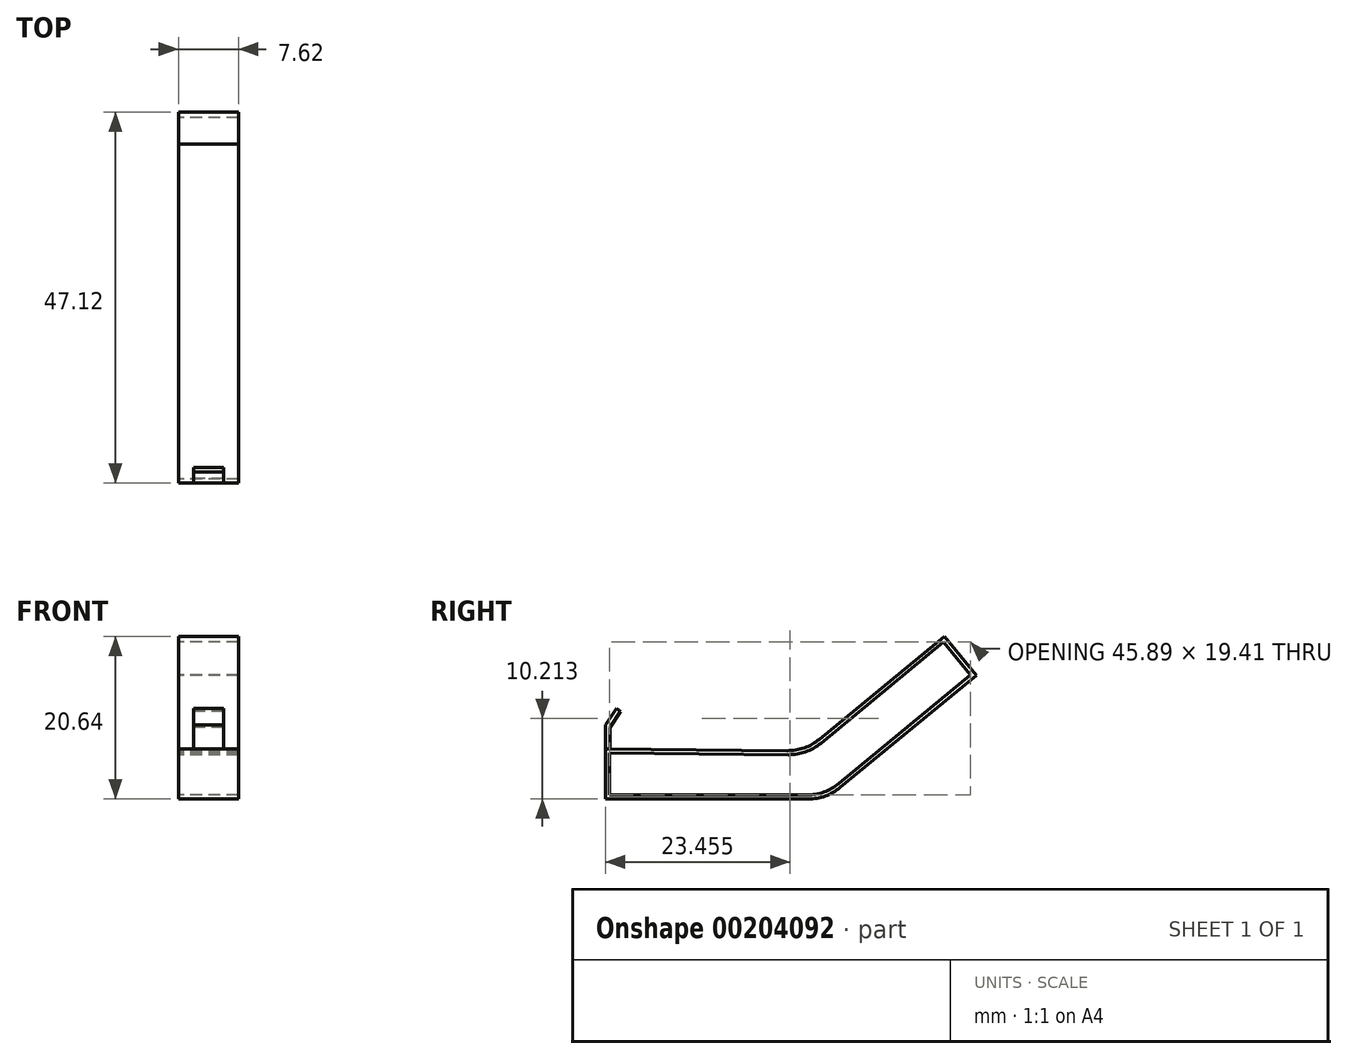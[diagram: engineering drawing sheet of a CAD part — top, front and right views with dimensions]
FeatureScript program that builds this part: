
annotation { "Feature Type Name" : "Feature", "Feature Type Description" : "" }
export const myFeature = defineFeature(function(context is Context, id is Id, definition is map)
    precondition{}
    {
        {
            var Q0;
            Q0=qCreatedBy(makeId("Right.planeOp"),FACE);
            var sketch = newSketch(context, id + "F0", { "sketchPlane" : qUnion([Q0])});
            skLineSegment(sketch, "E0", {"start": v(0, 0) * mm, "end": v(0, 6.35) * mm});
            skLineSegment(sketch, "E1", {"start": v(0, 6.35) * mm, "end": v(23.09, 6.13) * mm});
            skLineSegment(sketch, "E2", {"start": v(27.18, 7.58) * mm, "end": v(43.05, 20.64) * mm});
            skLineSegment(sketch, "E3", {"start": v(0, 0) * mm, "end": v(25.79, 0) * mm});
            skLineSegment(sketch, "E4", {"start": v(29.83, 1.45) * mm, "end": v(47.12, 15.69) * mm});
            skLineSegment(sketch, "E5", {"start": v(43.05, 20.64) * mm, "end": v(47.12, 15.69) * mm});
            skLineSegment(sketch, "E6.0", {"start": v(0, 5.84) * mm, "end": v(0, 5.84) * mm});
            skLineSegment(sketch, "E7.0", {"start": v(0.5, 0.5) * mm, "end": v(0.5, 5.84) * mm});
            skLineSegment(sketch, "E8.0", {"start": v(0.5, 0.5) * mm, "end": v(25.6, 0.5) * mm});
            skLineSegment(sketch, "E9.0", {"start": v(29.64, 1.96) * mm, "end": v(46.4, 15.75) * mm});
            skLineSegment(sketch, "E10.0", {"start": v(27.36, 7.07) * mm, "end": v(42.97, 19.92) * mm});
            skLineSegment(sketch, "E11.trimOffspring", {"start": v(0.5, 5.84) * mm, "end": v(23.27, 5.62) * mm});
            skLineSegment(sketch, "E12.trimOffspring", {"start": v(0.5, 6.35) * mm, "end": v(0.5, 6.35) * mm});
            skLineSegment(sketch, "E13", {"start": v(42.97, 19.92) * mm, "end": v(46.4, 15.75) * mm});
            skPoint(sketch, "E14.visualSharp", {"position": v(25.58, 5.6) * mm});
            skArc(sketch, "E14.filletArc", {"start": v(23.27, 5.62) * mm, "mid": v(25.44, 5.98) * mm, "end": v(27.36, 7.07) * mm});
            skPoint(sketch, "E15.visualSharp", {"position": v(25.4, 6.11) * mm});
            skArc(sketch, "E15.filletArc", {"start": v(23.09, 6.13) * mm, "mid": v(25.26, 6.5) * mm, "end": v(27.18, 7.58) * mm});
            skPoint(sketch, "E16.visualSharp", {"position": v(27.88, 0.5) * mm});
            skArc(sketch, "E16.filletArc", {"start": v(25.6, 0.5) * mm, "mid": v(27.75, 0.88) * mm, "end": v(29.64, 1.96) * mm});
            skPoint(sketch, "E17.visualSharp", {"position": v(28.07, 0) * mm});
            skArc(sketch, "E17.filletArc", {"start": v(25.79, 0) * mm, "mid": v(27.93, 0.37) * mm, "end": v(29.83, 1.45) * mm});
            skSolve(sketch);
        }
        {
            var Q0;
            Q0=qSketchRegion(id+"F0",true);
            var Q1;
            {var subQ3=sQuery(id+"F0.wireOp",EDGE,"E2");Q1=makeQuery(id+"F0.imprint","IMPRINT",FACE,{"disambiguationData":[TD([[makeQuery(id+"F0.imprint","IMPRINT",EDGE,{"derivedFrom":subQ3}),-1.0]])]});}
            extrude(context, id + "F1", {"entities" : qUnion([Q0, Q1]), "endBound" : BoundingType.SYMMETRIC, "depth" : 7.62 * mm});
        }
        {
            var Q0;
            Q0=qCreatedBy(makeId("Right.planeOp"),FACE);
            var sketch = newSketch(context, id + "F2", { "sketchPlane" : qUnion([Q0])});
            skLineSegment(sketch, "E18", {"start": v(0, 6.36) * mm, "end": v(0, 9.37) * mm});
            skLineSegment(sketch, "E19", {"start": v(0, 9.37) * mm, "end": v(1.39, 11.5) * mm});
            skLineSegment(sketch, "E20", {"start": v(1.39, 11.5) * mm, "end": v(1.94, 11.14) * mm});
            skLineSegment(sketch, "E21", {"start": v(1.94, 11.14) * mm, "end": v(0.6, 9.08) * mm});
            skLineSegment(sketch, "E22", {"start": v(0.6, 6.35) * mm, "end": v(0.6, 9.08) * mm});
            skLineSegment(sketch, "E23", {"start": v(0, 6.36) * mm, "end": v(0.6, 6.35) * mm});
            skSolve(sketch);
        }
        {
            var Q0;
            Q0=qSketchRegion(id+"F2",true);
            extrude(context, id + "F3", {"entities" : qUnion([Q0]), "endBound" : BoundingType.SYMMETRIC, "depth" : 3.8 * mm});
        }
    });
